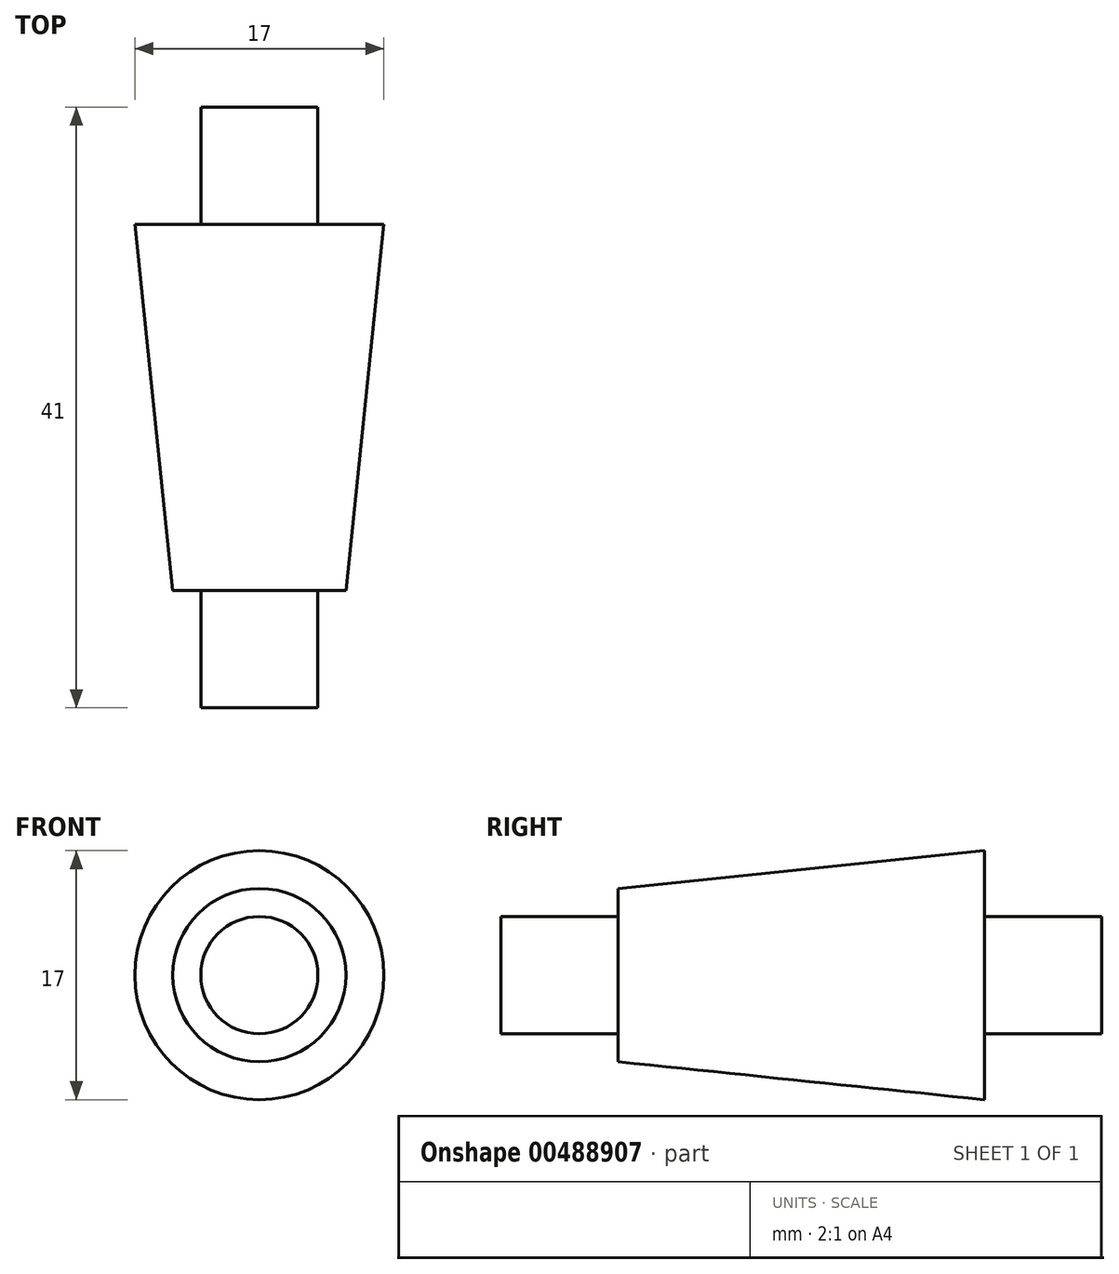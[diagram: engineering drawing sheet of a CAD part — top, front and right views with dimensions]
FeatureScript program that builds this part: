
annotation { "Feature Type Name" : "Feature", "Feature Type Description" : "" }
export const myFeature = defineFeature(function(context is Context, id is Id, definition is map)
    precondition{}
    {
        {
            var Q0;
            Q0=qCreatedBy(makeId("Right.planeOp"),FACE);
            var sketch = newSketch(context, id + "F0", { "sketchPlane" : qUnion([Q0])});
            skLineSegment(sketch, "E0", {"start": v(0, 0) * mm, "end": v(41, 0) * mm});
            skLineSegment(sketch, "E1", {"start": v(41, 0) * mm, "end": v(41, 4) * mm});
            skLineSegment(sketch, "E2", {"start": v(41, 4) * mm, "end": v(33, 4) * mm});
            skLineSegment(sketch, "E3", {"start": v(33, 4) * mm, "end": v(33, 8.5) * mm});
            skLineSegment(sketch, "E4", {"start": v(33, 8.5) * mm, "end": v(8, 5.91) * mm});
            skLineSegment(sketch, "E5", {"start": v(0, 0) * mm, "end": v(0, 4) * mm});
            skLineSegment(sketch, "E6", {"start": v(0, 4) * mm, "end": v(8, 4) * mm});
            skLineSegment(sketch, "E7", {"start": v(8, 4) * mm, "end": v(8, 5.91) * mm});
            skSolve(sketch);
        }
        {
            var Q0;
            Q0=makeQuery(id+"F0.imprint","IMPRINT",FACE,{"disambiguationData":[TD([[makeQuery(id+"F0.imprint","IMPRINT",EDGE,{"derivedFrom":sQuery(id+"F0.wireOp",EDGE,"E0")}),1.0]])]});
            var Q1;
            Q1=sQuery(id+"F0.wireOp",EDGE,"E0");
            revolve(context, id + "F1", {"entities" : qUnion([Q0]), "axis" : qUnion([Q1]), "revolveType" : RevolveType.FULL});
        }
    });
